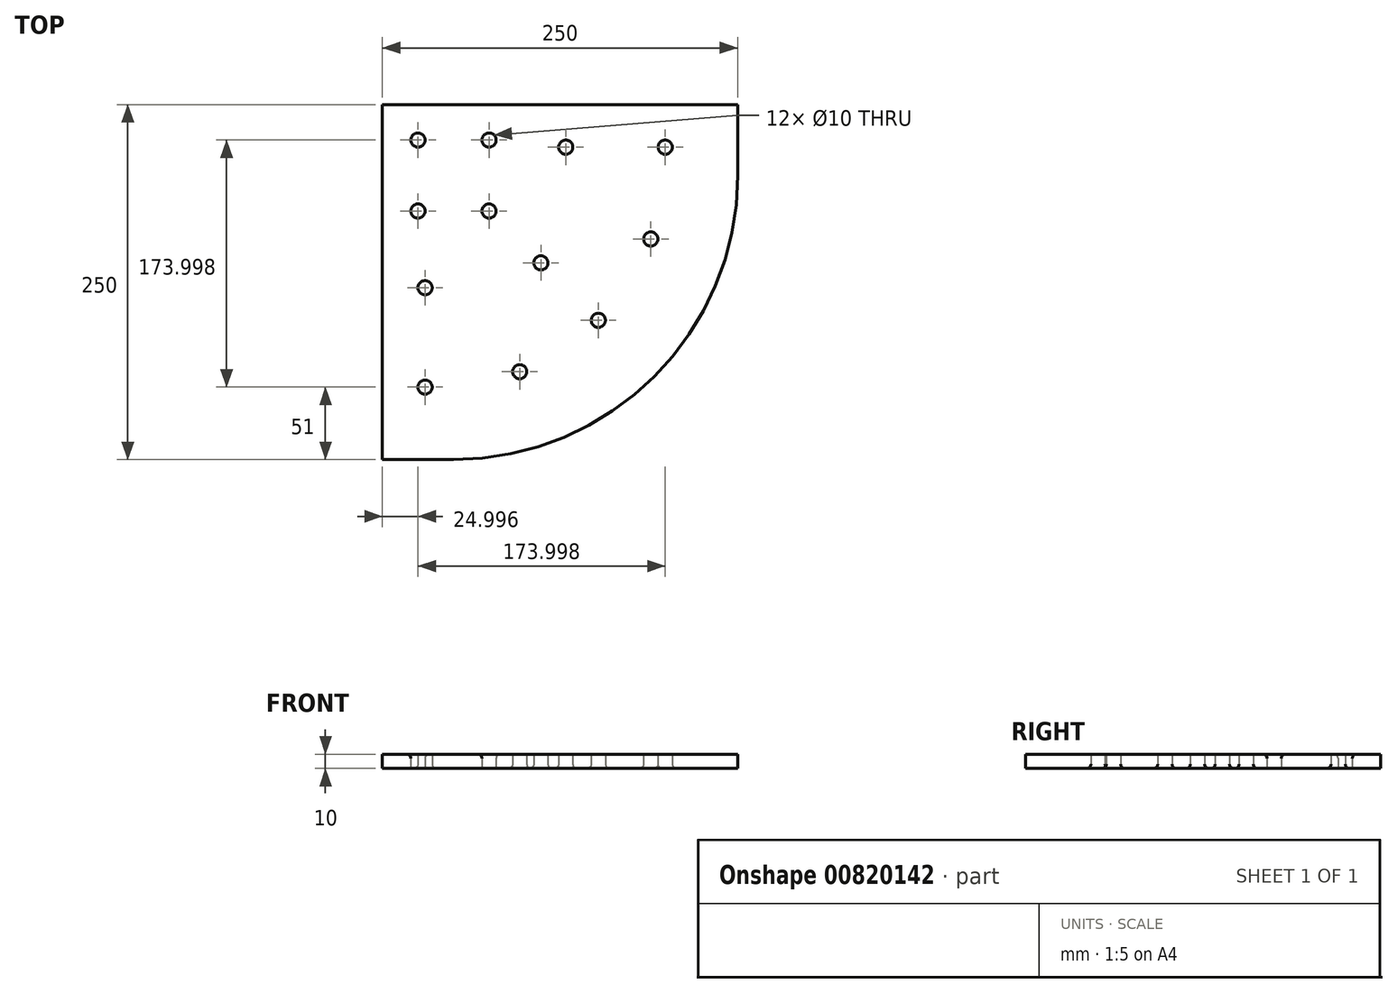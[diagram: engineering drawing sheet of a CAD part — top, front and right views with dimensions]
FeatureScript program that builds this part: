
annotation { "Feature Type Name" : "Feature", "Feature Type Description" : "" }
export const myFeature = defineFeature(function(context is Context, id is Id, definition is map)
    precondition{}
    {
        {
            var Q0;
            Q0=qCreatedBy(makeId("Top.planeOp"),FACE);
            var sketch = newSketch(context, id + "F0", { "sketchPlane" : qUnion([Q0])});
            skLineSegment(sketch, "E0.bottom", {"start": v(-156.26, 147.44) * mm, "end": v(93.74, 147.44) * mm});
            skLineSegment(sketch, "E0.top", {"start": v(-156.26, -102.56) * mm, "end": v(-106.26, -102.56) * mm});
            skLineSegment(sketch, "E0.left", {"start": v(-156.26, 147.44) * mm, "end": v(-156.26, -102.56) * mm});
            skLineSegment(sketch, "E0.right", {"start": v(93.74, 147.44) * mm, "end": v(93.74, 97.44) * mm});
            skPoint(sketch, "E1.visualSharp", {"position": v(93.74, -102.56) * mm});
            skArc(sketch, "E1.filletArc", {"start": v(-106.26, -102.56) * mm, "mid": v(35.16, -43.98) * mm, "end": v(93.74, 97.44) * mm});
            skCircle(sketch, "E2", {"center": v(-27.27, 117.44) * mm, "radius": 5 * mm});
            skCircle(sketch, "E3", {"center": v(42.73, 117.44) * mm, "radius": 5 * mm});
            skCircle(sketch, "E4", {"center": v(-126.26, 18.44) * mm, "radius": 5 * mm});
            skCircle(sketch, "E5", {"center": v(-126.26, -51.56) * mm, "radius": 5 * mm});
            skCircle(sketch, "E6", {"center": v(-131.26, 122.44) * mm, "radius": 5 * mm});
            skCircle(sketch, "E7", {"center": v(-4.33, -4.5) * mm, "radius": 5 * mm});
            skCircle(sketch, "E8", {"center": v(32.58, 52.74) * mm, "radius": 5 * mm});
            skCircle(sketch, "E9", {"center": v(-59.67, -40.68) * mm, "radius": 5 * mm});
            skCircle(sketch, "E10", {"center": v(-81.26, 122.44) * mm, "radius": 5 * mm});
            skCircle(sketch, "E11", {"center": v(-131.26, 72.44) * mm, "radius": 5 * mm});
            skCircle(sketch, "E12", {"center": v(-81.26, 72.44) * mm, "radius": 5 * mm});
            skCircle(sketch, "E13", {"center": v(-44.77, 35.95) * mm, "radius": 5 * mm});
            skSolve(sketch);
        }
        {
            var Q0;
            Q0=makeQuery(id+"F0.imprint","IMPRINT",FACE,{"disambiguationData":[TD([[makeQuery(id+"F0.imprint","IMPRINT",EDGE,{"derivedFrom":sQuery(id+"F0.wireOp",EDGE,"E0.bottom")}),-1.0]])]});
            extrude(context, id + "F1", {"entities" : qUnion([Q0]), "depth" : 10 * mm, "offsetDistance" : 25 * mm});
        }
        {
            var Q0;
            Q0=makeQuery(id+"F1.opExtrude","CAP_EDGE",EDGE,{"disambiguationData":[OSD([sQuery(id+"F0.wireOp",EDGE,"E6")])],"isStart":false});
            var Q1;
            Q1=makeQuery(id+"F1.opExtrude","CAP_EDGE",EDGE,{"disambiguationData":[OSD([sQuery(id+"F0.wireOp",EDGE,"E10")])],"isStart":false});
            var Q2;
            Q2=makeQuery(id+"F1.opExtrude","CAP_EDGE",EDGE,{"disambiguationData":[OSD([sQuery(id+"F0.wireOp",EDGE,"E11")])],"isStart":false});
            var Q3;
            Q3=makeQuery(id+"F1.opExtrude","CAP_EDGE",EDGE,{"disambiguationData":[OSD([sQuery(id+"F0.wireOp",EDGE,"E12")])],"isStart":false});
            fillet(context, id + "F2", {"entities" : qUnion([Q0, Q1, Q2, Q3]), "radius" : 3 * mm, "tangentPropagation" : true, "allowEdgeOverflow" : false});
        }
        {
            var Q0;
            Q0=makeQuery(id+"F1.opExtrude","CAP_EDGE",EDGE,{"disambiguationData":[OSD([sQuery(id+"F0.wireOp",EDGE,"E5")])],"isStart":true});
            var Q1;
            Q1=makeQuery(id+"F1.opExtrude","CAP_EDGE",EDGE,{"disambiguationData":[OSD([sQuery(id+"F0.wireOp",EDGE,"E9")])],"isStart":true});
            var Q2;
            Q2=makeQuery(id+"F1.opExtrude","CAP_EDGE",EDGE,{"disambiguationData":[OSD([sQuery(id+"F0.wireOp",EDGE,"E7")])],"isStart":true});
            var Q3;
            Q3=makeQuery(id+"F1.opExtrude","CAP_EDGE",EDGE,{"disambiguationData":[OSD([sQuery(id+"F0.wireOp",EDGE,"E8")])],"isStart":true});
            var Q4;
            Q4=makeQuery(id+"F1.opExtrude","CAP_EDGE",EDGE,{"disambiguationData":[OSD([sQuery(id+"F0.wireOp",EDGE,"E3")])],"isStart":true});
            var Q5;
            Q5=makeQuery(id+"F1.opExtrude","CAP_EDGE",EDGE,{"disambiguationData":[OSD([sQuery(id+"F0.wireOp",EDGE,"E2")])],"isStart":true});
            var Q6;
            Q6=makeQuery(id+"F1.opExtrude","CAP_EDGE",EDGE,{"disambiguationData":[OSD([sQuery(id+"F0.wireOp",EDGE,"E13")])],"isStart":true});
            var Q7;
            Q7=makeQuery(id+"F1.opExtrude","CAP_EDGE",EDGE,{"disambiguationData":[OSD([sQuery(id+"F0.wireOp",EDGE,"E4")])],"isStart":true});
            fillet(context, id + "F3", {"entities" : qUnion([Q0, Q1, Q2, Q3, Q4, Q5, Q6, Q7]), "radius" : 3 * mm, "tangentPropagation" : true, "allowEdgeOverflow" : false});
        }
    });
